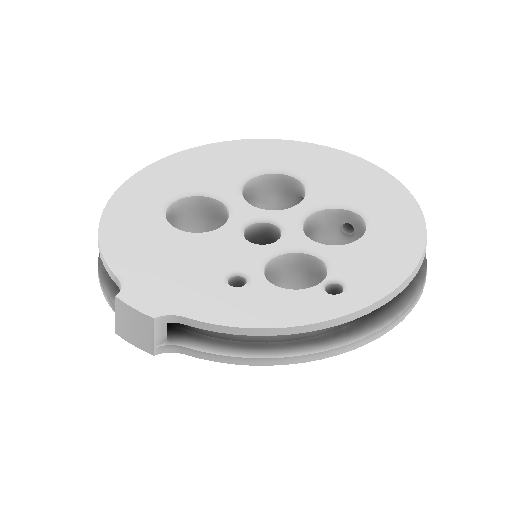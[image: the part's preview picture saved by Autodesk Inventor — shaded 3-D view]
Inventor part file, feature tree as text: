
AUTODESK INVENTOR PART (.ipt)
format: ipt  version: 2022 (Build 260153000, 153)  size: 318,464 bytes
history: native  units: mm
features: extrude x8, sketch x7, plane x3, fillet x2, pattern_circular x1, mirror x1, projected_geometry x1
ambient origin geometry x8: Origin, YZ Plane, XZ Plane, XY Plane, X Axis, Y Axis, Z Axis, Center Point
bodies: Solid1 (feature_tree)
feature tree (23):
  extrude  "Extrusion1"  Depth=30.0mm
  extrude  "Extrusion2"  Depth=3.0mm TaperAngle=0.0deg
  pattern_circular  "Circular Pattern1"  Count=5 Angle=360.0deg
  plane  "Work Plane1"
  plane  "Work Plane2"
  extrude  "Extrusion3"  [1 undecoded]
  extrude  "Extrusion4"  Depth=3.0mm
  fillet  "Fillet1"  Radius=1.7mm
  plane  "Work Plane3"
  extrude  "Extrusion5"  Depth=10.0mm TaperAngle=0.0deg
  mirror  "Mirror1"
  sketch  "Sketch6"  dims[d13=9.599311mm d14=-9.599311mm]
  extrude  "Extrusion6"  Depth=3.0mm
  extrude  "Extrusion7"  Depth=3.0mm
  extrude  "Extrusion8"  Depth=3.0mm
  fillet  "Fillet2"  Radius=10.0mm
  sketch  "Sketch1"  dims[d0=4.2mm d2=30.0mm]
  sketch  "Sketch2"  dims[d3=4.0mm d4=3.0mm d5=0.0mm]
  sketch  "Sketch3"  dims[d6=7.0mm]
  sketch  "Sketch4"  dims[d7=8.0mm]
  sketch  "Sketch5"  dims[d8=10.0mm d9=0.0mm d10=50.0mm d11=360.0deg]
  projected_geometry  "Projected Loop1"
  sketch  "Sketch7"  dims[d15=1.5mm d16=1.5mm d17=1.7mm d18=10.0mm d19=0.0mm d20=1.5mm d21=1.5mm d22=1.7mm d23=10.0mm d24=0.0mm d25=1.0mm d26=36.0mm d27=1.0mm d28=0.0mm d29=2.1mm d30=13.0mm d31=1.9mm d32=2.1mm d33=8.4mm d35=5.0mm d36=0.0mm d37=100.0mm d38=0.0mm d39=4.5mm d40=3.0mm d41=3.0mm d42=2.0mm d43=5.0mm d44=0.0mm d45=3.0mm]
note: 1 required parameter value undecoded (feature->parameter linkage not recoverable at this tier; creation-order binding heuristic only, values carry confidence <= 0.55)
